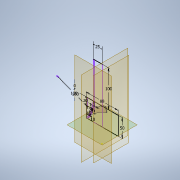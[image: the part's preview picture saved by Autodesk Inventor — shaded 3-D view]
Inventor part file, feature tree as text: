
AUTODESK INVENTOR PART (.ipt)
format: ipt  version: 2022.3 (Build 263350000, 350)  size: 439,296 bytes
history: native  units: mm
features: sketch x11, extrude x9, revolve x5, plane x4, hole x3, pattern_circular x2, mirror x2
ambient origin geometry x8: Origin, YZ Plane, XZ Plane, XY Plane, X Axis, Y Axis, Z Axis, Center Point
bodies: Solid1 (feature_tree)
feature tree (36):
  extrude  "Extrusion1"  Depth=4.0mm
  sketch  "Sketch2"  dims[d2=40.0mm d3=0.0mm d4=88.0mm]
  revolve  "Revolution1"  [1 undecoded]
  plane  "Work Plane1"
  extrude  "Extrusion2"  Depth=100.0mm
  sketch  "Sketch18"  dims[d5=50.0mm d8=100.0mm]
  extrude  "Extrusion11"  Depth=100.0mm
  extrude  "Extrusion12"  Depth=100.0mm
  extrude  "Extrusion13"  [1 undecoded]
  pattern_circular  "Circular Pattern2"  [2 undecoded]
  revolve  "Revolution4"  [1 undecoded]
  plane  "Work Plane3"
  plane  "Work Plane4"
  hole  "Hole5"  [1 undecoded]
  hole  "Hole6"  [1 undecoded]
  mirror  "Mirror1"
  mirror  "Mirror2"
  extrude  "Extrusion15"  Depth=50.0mm
  plane  "Work Plane5"
  sketch  "Sketch24"  dims[d16=75.0mm]
  revolve  "Revolution7"  [1 undecoded]
  hole  "Hole8"  [1 undecoded]
  pattern_circular  "Circular Pattern4"  Count=3  [1 undecoded]
  extrude  "Extrusion16"  Depth=50.0mm
  extrude  "Extrusion17"  Depth=50.0mm
  revolve  "Revolution15"  [1 undecoded]
  revolve  "Revolution16"  [1 undecoded]
  extrude  "Extrusion18"  Depth=50.0mm
  sketch  "Sketch1"  dims[d0=80.0mm d1=4.0mm]
  sketch  "Sketch19"  dims[d9=25.0mm d10=100.0mm]
  sketch  "Sketch20"  dims[d11=4.0mm d12=100.0mm]
  sketch  "Sketch21"  dims[d13=360.0deg d14=-45.0mm]
  sketch  "Sketch22"  dims[d15=5.0mm]
  sketch  "Sketch25"  dims[d17=75.0mm]
  sketch  "Sketch26"  dims[d18=5.0mm]
  sketch  "Sketch27"  dims[d19=15.0mm d20=5.2mm d21=5.0mm d22=0.0mm d79=0.0mm d106=4.0mm d107=10.0mm d108=30.0mm d109=0.0mm d110=10.0mm d111=30.0mm d112=0.0mm d113=1.0mm d114=10.0mm d115=1.0mm d116=3.0mm d117=1.0mm d118=5.0mm d119=1.0mm d120=4.0mm d121=1.0mm d122=5.0mm d123=10.0mm d124=90.0deg d131=10.0mm d132=0.0mm d133=1.0mm d134=3.0mm d135=60.0mm d136=360.0deg d138=2.0mm d139=5.0mm d140=2.0mm d141=5.0mm d142=90.0deg d143=25.0mm d144=25.0mm d145=30.0mm d146=3.4mm d147=6.0mm d148=5.9mm d149=2.0mm d150=90.0deg d151=4.2mm d152=0.0mm d153=30.0mm d154=180.0deg d155=3.4mm d156=6.0mm d157=5.9mm d158=2.0mm d159=90.0deg d160=4.2mm d161=0.0mm d165=4.0mm d166=10.0mm d167=0.0mm d168=6.6mm d181=10.0mm d182=10.0mm d183=90.0deg d184=5.0mm d185=2.0mm d186=2.2mm d187=6.0mm d188=3.1mm d189=4.1mm d190=90.0deg d191=0.9mm d192=0.0mm d193=20.0mm d194=90.0deg d196=20.0mm d197=20.0mm d198=15.0mm d199=10.0mm d202=10.0mm d203=10.0mm d204=10.0mm d205=1.0mm d206=5.0mm d207=2.0mm d208=5.0mm d209=1.0mm d215=120.0mm d216=0.0mm d217=50.0mm d218=0.0mm d219=300.0deg d220=360.0deg d221=0.0mm d222=0.0mm d125=0.872665mm d126=0.872665mm d137=14.3117mm d164=2.25mm d212=0.872665mm d213=0.872665mm]
note: 12 required parameter values undecoded (feature->parameter linkage not recoverable at this tier; creation-order binding heuristic only, values carry confidence <= 0.55)